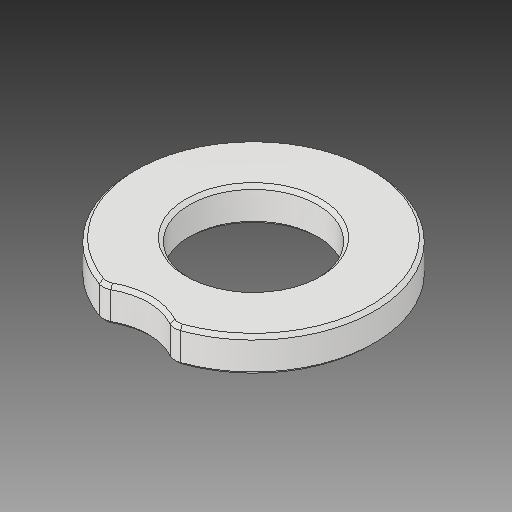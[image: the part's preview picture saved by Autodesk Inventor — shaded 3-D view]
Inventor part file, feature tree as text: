
AUTODESK INVENTOR PART (.ipt)
format: ipt  version: 2019.4 (Build 234330000, 330)  size: 161,280 bytes
history: native  units: mm
features: chamfer x2, extrude x1, fillet x1, sketch x1
ambient origin geometry x8: Origin, YZ Plane, XZ Plane, XY Plane, X Axis, Y Axis, Z Axis, Center Point
bodies: Solid1 (feature_tree)
feature tree (5):
  extrude  "Extrusion1"  Depth=10.0mm
  fillet  "Fillet1"  Radius=40.0mm
  chamfer  "Chamfer1"  Angle=45.0deg  [1 undecoded]
  chamfer  "Chamfer2"  Distance=20.0mm
  sketch  "Sketch1"  dims[d0=18.5mm d2=3.4mm d4=40.0mm d6=360.0deg d8=45.0deg d10=20.0mm d11=10.0mm d12=5.0mm d13=0.0mm d14=2.0mm d24=0.5mm d25=2.0mm d26=45.0deg d30=7.5mm d31=3.75mm d32=0.5mm d33=2.0mm d34=45.0deg]
note: 1 required parameter value undecoded (feature->parameter linkage not recoverable at this tier; creation-order binding heuristic only, values carry confidence <= 0.55)
